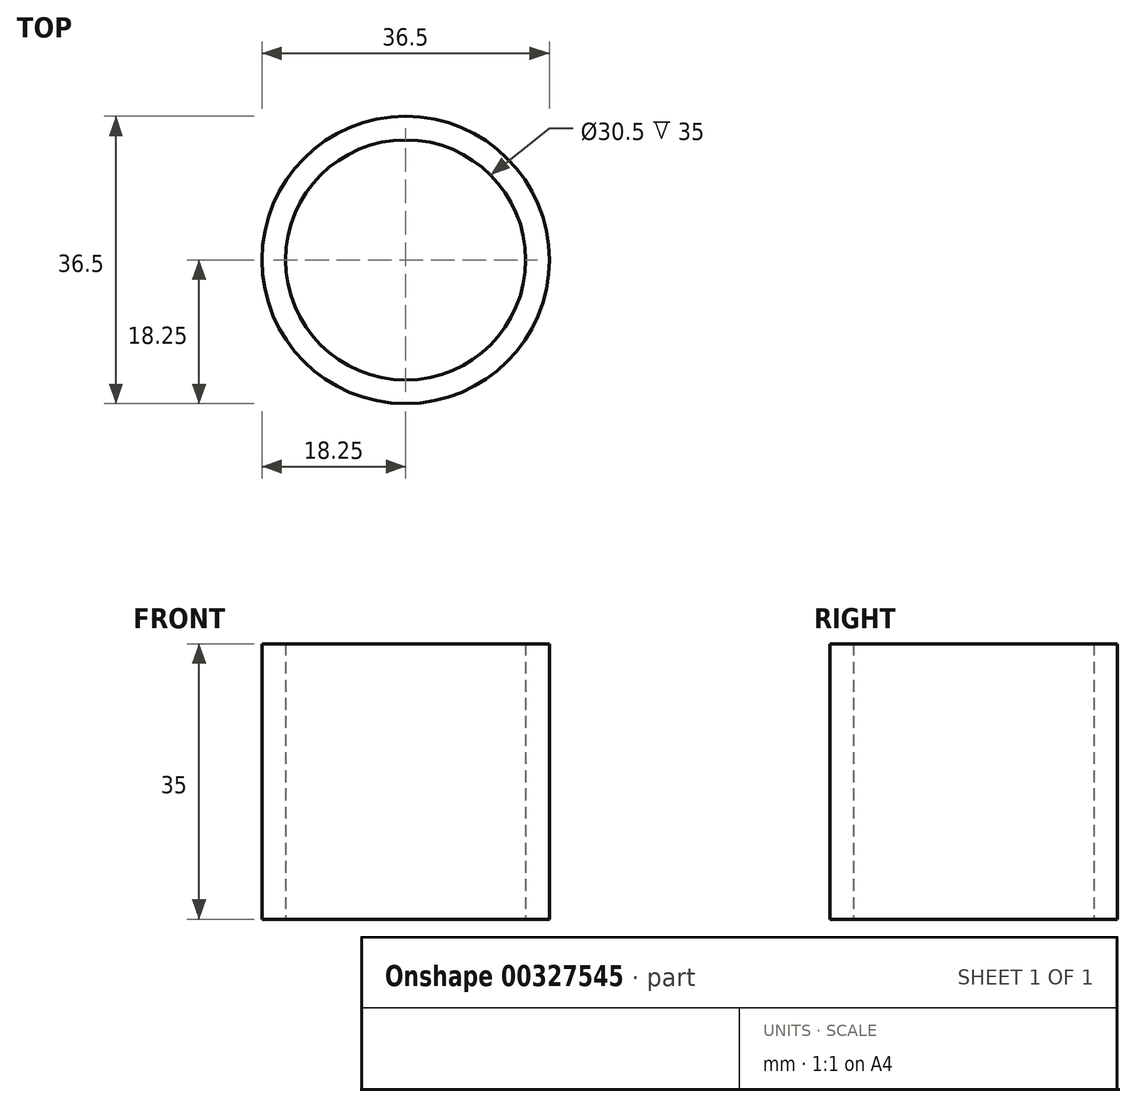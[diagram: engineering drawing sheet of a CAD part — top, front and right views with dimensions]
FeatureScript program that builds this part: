
annotation { "Feature Type Name" : "Feature", "Feature Type Description" : "" }
export const myFeature = defineFeature(function(context is Context, id is Id, definition is map)
    precondition{}
    {
        {
            var Q0;
            Q0=qCreatedBy(makeId("Top.planeOp"),FACE);
            var sketch = newSketch(context, id + "F0", { "sketchPlane" : qUnion([Q0])});
            skCircle(sketch, "E0", {"center": v(0, 0) * mm, "radius": 18.25 * mm});
            skCircle(sketch, "E1", {"center": v(0, 0) * mm, "radius": 15.25 * mm});
            skCircle(sketch, "E2", {"center": v(0, 0) * mm, "radius": 24.6 * mm, "construction": true});
            skSolve(sketch);
        }
        {
            var Q0;
            Q0 = qSketchRegion(id + "F0", true);
            var Q1;
            Q1=sQuery(id+"F0.wireOp",EDGE,"E0");
            extrude(context, id + "F1", {"entities" : qUnion([Q0]), "surfaceEntities" : qUnion([Q1]), "depth" : 35 * mm, "symmetric" : true});
        }
    });
